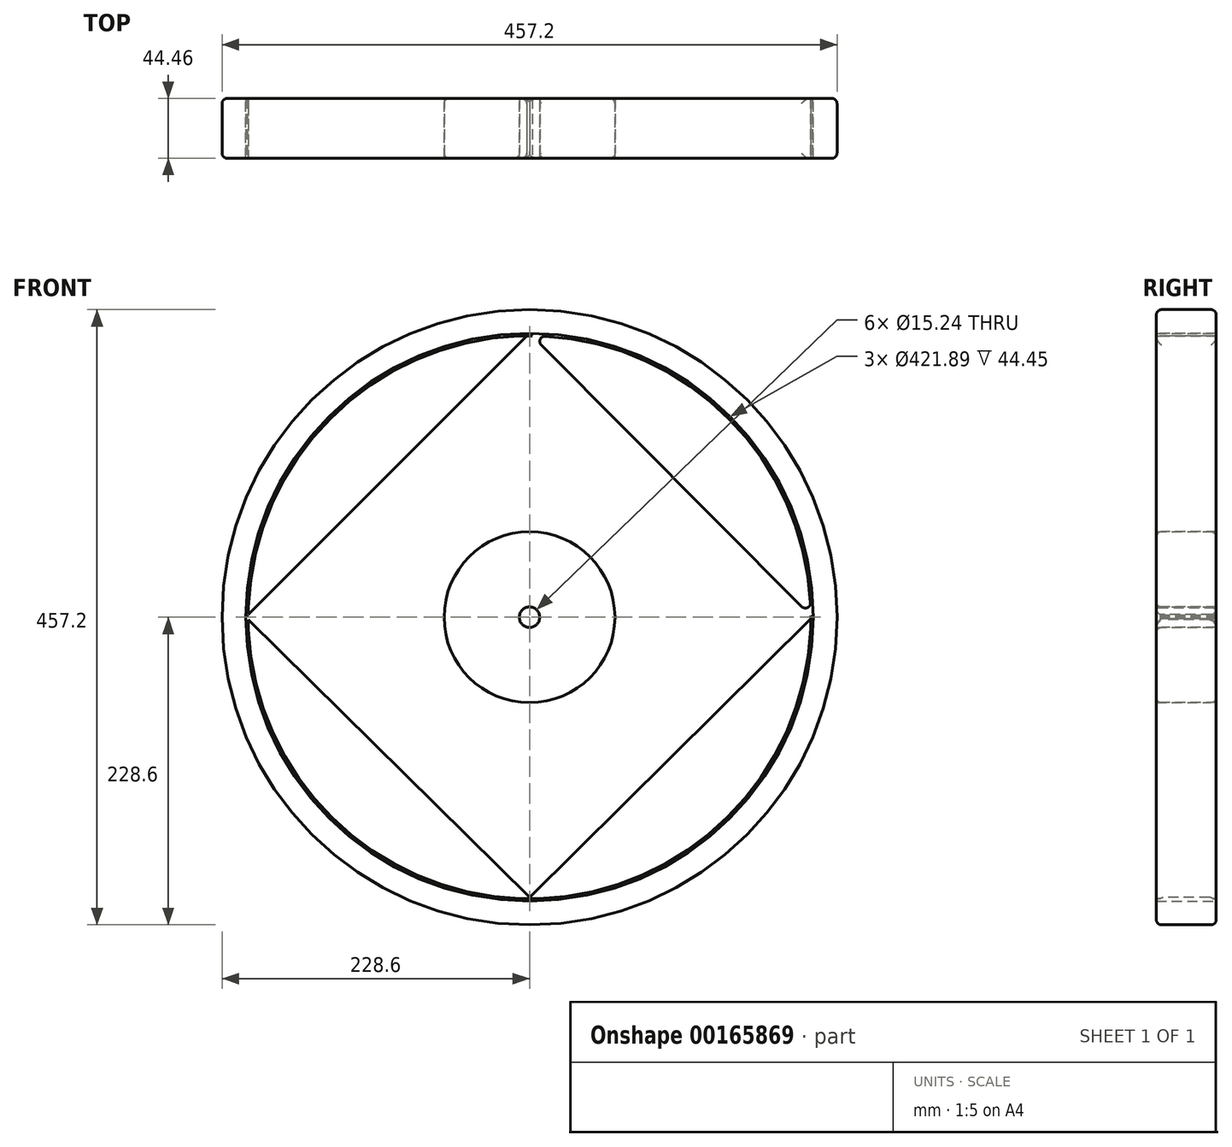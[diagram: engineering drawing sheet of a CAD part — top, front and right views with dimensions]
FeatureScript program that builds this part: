
annotation { "Feature Type Name" : "Feature", "Feature Type Description" : "" }
export const myFeature = defineFeature(function(context is Context, id is Id, definition is map)
    precondition{}
    {
        {
            var Q0;
            Q0=qCreatedBy(makeId("Front.planeOp"),FACE);
            var sketch = newSketch(context, id + "F0", { "sketchPlane" : qUnion([Q0])});
            skCircle(sketch, "E0", {"center": v(0, 0) * mm, "radius": 228.6 * mm});
            skCircle(sketch, "E1", {"center": v(0, 0) * mm, "radius": 7.62 * mm});
            skLineSegment(sketch, "E2", {"start": v(0, 0) * mm, "end": v(0, 228.6) * mm});
            skLineSegment(sketch, "E3", {"start": v(0, 0) * mm, "end": v(0, -228.6) * mm});
            skLineSegment(sketch, "E4", {"start": v(0, 0) * mm, "end": v(-228.6, 0) * mm});
            skLineSegment(sketch, "E5", {"start": v(0, 0) * mm, "end": v(228.6, 0) * mm});
            skCircle(sketch, "E6", {"center": v(0, 0) * mm, "radius": 63.5 * mm});
            skCircle(sketch, "E7", {"center": v(0, 0) * mm, "radius": 210.95 * mm});
            skSolve(sketch);
        }
        {
            var Q0;
            Q0 = qSketchRegion(id + "F0", true);
            var Q1;
            {var subQ0=sQuery(id+"F0.wireOp",EDGE,"E2");var subQ1=sQuery(id+"F0.wireOp",EDGE,"E0");var subQ2=makeQuery(id+"F0.imprint","INTERSECT",VERTEX,{"derivedFrom":[subQ1,subQ0]});Q1=makeQuery(id+"F0.imprint","IMPRINT",FACE,{"disambiguationData":[TD([[makeQuery(id+"F0.imprint","IMPRINT",EDGE,{"disambiguationData":[TD([[subQ2,-1.0]])],"derivedFrom":subQ1}),1.0]])]});}
            var Q2;
            {var subQ0=sQuery(id+"F0.wireOp",EDGE,"E2");var subQ1=sQuery(id+"F0.wireOp",EDGE,"E1");var subQ2=makeQuery(id+"F0.imprint","INTERSECT",VERTEX,{"derivedFrom":[subQ1,subQ0]});Q2=makeQuery(id+"F0.imprint","IMPRINT",FACE,{"disambiguationData":[TD([[makeQuery(id+"F0.imprint","IMPRINT",EDGE,{"disambiguationData":[TD([[subQ2,-1.0]])],"derivedFrom":subQ1}),-1.0]])]});}
            var Q3;
            {var subQ0=sQuery(id+"F0.wireOp",EDGE,"E2");var subQ1=sQuery(id+"F0.wireOp",EDGE,"E1");var subQ2=makeQuery(id+"F0.imprint","INTERSECT",VERTEX,{"derivedFrom":[subQ1,subQ0]});Q3=makeQuery(id+"F0.imprint","IMPRINT",FACE,{"disambiguationData":[TD([[makeQuery(id+"F0.imprint","IMPRINT",EDGE,{"disambiguationData":[TD([[subQ2,1.0]])],"derivedFrom":subQ1}),-1.0]])]});}
            var Q4;
            {var subQ0=sQuery(id+"F0.wireOp",EDGE,"E5");var subQ1=sQuery(id+"F0.wireOp",EDGE,"E1");var subQ2=makeQuery(id+"F0.imprint","INTERSECT",VERTEX,{"derivedFrom":[subQ1,subQ0]});Q4=makeQuery(id+"F0.imprint","IMPRINT",FACE,{"disambiguationData":[TD([[makeQuery(id+"F0.imprint","IMPRINT",EDGE,{"disambiguationData":[TD([[subQ2,1.0]])],"derivedFrom":subQ1}),-1.0]])]});}
            var Q5;
            {var subQ0=sQuery(id+"F0.wireOp",EDGE,"E4");var subQ1=sQuery(id+"F0.wireOp",EDGE,"E1");var subQ2=makeQuery(id+"F0.imprint","INTERSECT",VERTEX,{"derivedFrom":[subQ1,subQ0]});Q5=makeQuery(id+"F0.imprint","IMPRINT",FACE,{"disambiguationData":[TD([[makeQuery(id+"F0.imprint","IMPRINT",EDGE,{"disambiguationData":[TD([[subQ2,-1.0]])],"derivedFrom":subQ1}),-1.0]])]});}
            extrude(context, id + "F1", {"entities" : qUnion([Q0, Q1, Q2, Q3, Q4, Q5]), "endBound" : BoundingType.SYMMETRIC, "depth" : 44.45 * mm});
        }
        {
            var Q0;
            Q0=makeQuery(id+"F1.opExtrude","CAP_FACE",FACE,{"disambiguationData":[OSD([sQuery(id+"F0.wireOp",EDGE,"E1"),sQuery(id+"F0.wireOp",EDGE,"E6")])],"isStart":false});
            var sketch = newSketch(context, id + "F2", { "sketchPlane" : qUnion([Q0])});
            skLineSegment(sketch, "E8", {"start": v(-209.14, 0) * mm, "end": v(-211.01, 0) * mm});
            skLineSegment(sketch, "E9", {"start": v(209.14, 0) * mm, "end": v(210.23, 0) * mm});
            skLineSegment(sketch, "E10", {"start": v(0, 209.14) * mm, "end": v(0, 211.07) * mm});
            skLineSegment(sketch, "E11", {"start": v(0, -208.2) * mm, "end": v(-211.01, 0) * mm});
            skLineSegment(sketch, "E12", {"start": v(-211.01, 0) * mm, "end": v(0, 211.07) * mm});
            skLineSegment(sketch, "E13", {"start": v(0, 211.07) * mm, "end": v(210.23, 0) * mm});
            skLineSegment(sketch, "E14", {"start": v(210.23, 0) * mm, "end": v(0, -208.2) * mm});
            skCircle(sketch, "E15", {"center": v(0, 0) * mm, "radius": 209.14 * mm});
            skSolve(sketch);
        }
        {
            var Q0;
            {var subQ0=sQuery(id+"F2.wireOp",EDGE,"E14");var subQ1=sQuery(id+"F2.wireOp",EDGE,"E11");var subQ2=makeQuery(id+"F2.imprint","INTERSECT",VERTEX,{"derivedFrom":[subQ1,subQ0]});Q0=makeQuery(id+"F2.imprint","IMPRINT",FACE,{"disambiguationData":[TD([[makeQuery(id+"F2.imprint","IMPRINT",EDGE,{"disambiguationData":[TD([[subQ2,-1.0]])],"derivedFrom":subQ1}),1.0]])]});}
            var Q1;
            {var subQ0=sQuery(id+"F2.wireOp",EDGE,"E15");var subQ1=sQuery(id+"F2.wireOp",EDGE,"E12");var subQ2=makeQuery(id+"F2.imprint","INTERSECT",VERTEX,{"disambiguationData":[OD(0.0)],"derivedFrom":[subQ1,subQ0]});Q1=makeQuery(id+"F2.imprint","IMPRINT",FACE,{"disambiguationData":[TD([[makeQuery(id+"F2.imprint","IMPRINT",EDGE,{"disambiguationData":[TD([[subQ2,-1.0]])],"derivedFrom":subQ1}),1.0]])]});}
            var Q2;
            {var subQ0=sQuery(id+"F2.wireOp",EDGE,"E15");var subQ1=sQuery(id+"F2.wireOp",EDGE,"E13");var subQ2=makeQuery(id+"F2.imprint","INTERSECT",VERTEX,{"disambiguationData":[OD(0.0)],"derivedFrom":[subQ1,subQ0]});Q2=makeQuery(id+"F2.imprint","IMPRINT",FACE,{"disambiguationData":[TD([[makeQuery(id+"F2.imprint","IMPRINT",EDGE,{"disambiguationData":[TD([[subQ2,-1.0]])],"derivedFrom":subQ1}),1.0]])]});}
            var Q3;
            {var subQ0=sQuery(id+"F2.wireOp",EDGE,"E8");Q3=makeQuery(id+"F2.imprint","IMPRINT",FACE,{"disambiguationData":[TD([[makeQuery(id+"F2.imprint","IMPRINT",EDGE,{"derivedFrom":subQ0}),1.0]])]});}
            var Q4;
            {var subQ0=sQuery(id+"F2.wireOp",EDGE,"E8");Q4=makeQuery(id+"F2.imprint","IMPRINT",FACE,{"disambiguationData":[TD([[makeQuery(id+"F2.imprint","IMPRINT",EDGE,{"derivedFrom":subQ0}),-1.0]])]});}
            var Q5;
            {var subQ0=sQuery(id+"F2.wireOp",EDGE,"E9");Q5=makeQuery(id+"F2.imprint","IMPRINT",FACE,{"disambiguationData":[TD([[makeQuery(id+"F2.imprint","IMPRINT",EDGE,{"derivedFrom":subQ0}),1.0]])]});}
            var Q6;
            {var subQ0=sQuery(id+"F2.wireOp",EDGE,"E9");Q6=makeQuery(id+"F2.imprint","IMPRINT",FACE,{"disambiguationData":[TD([[makeQuery(id+"F2.imprint","IMPRINT",EDGE,{"derivedFrom":subQ0}),-1.0]])]});}
            var Q7;
            {var subQ0=sQuery(id+"F2.wireOp",EDGE,"E10");Q7=makeQuery(id+"F2.imprint","IMPRINT",FACE,{"disambiguationData":[TD([[makeQuery(id+"F2.imprint","IMPRINT",EDGE,{"derivedFrom":subQ0}),1.0]])]});}
            var Q8;
            {var subQ0=sQuery(id+"F2.wireOp",EDGE,"E10");Q8=makeQuery(id+"F2.imprint","IMPRINT",FACE,{"disambiguationData":[TD([[makeQuery(id+"F2.imprint","IMPRINT",EDGE,{"derivedFrom":subQ0}),-1.0]])]});}
            var Q9;
            Q9=makeQuery(id+"F2.imprint","IMPRINT",FACE,{"disambiguationData":[TD([[makeQuery(id+"F2.imprint","IMPRINT",EDGE,{"derivedFrom":makeQuery(id+"F1.opExtrude","CAP_EDGE",EDGE,{"disambiguationData":[OSD([sQuery(id+"F0.wireOp",EDGE,"E1")])],"isStart":false})}),-1.0]])]});
            extrude(context, id + "F3", {"entities" : qUnion([Q0, Q1, Q2, Q3, Q4, Q5, Q6, Q7, Q8, Q9]), "oppositeDirection" : true, "depth" : 44.45 * mm});
        }
        {
            var Q0;
            {var subQ0=sQuery(id+"F2.wireOp",EDGE,"E15");var subQ1=sQuery(id+"F2.wireOp",EDGE,"E13");Q0=makeQuery(id+"F3.opExtrude","SWEPT_EDGE",EDGE,{"disambiguationData":[OSD([subQ1,subQ0]),TDD([makeQuery(id+"F2.imprint","INTERSECT",VERTEX,{"disambiguationData":[OD(1.0)],"derivedFrom":[subQ1,subQ0]})]),ownerDisambiguation([makeQuery(id+"F3.opExtrude","SWEPT_BODY",BODY,{"disambiguationData":[OSD([subQ1,subQ0])]})])]});}
            var Q1;
            {var subQ0=sQuery(id+"F2.wireOp",EDGE,"E15");var subQ1=sQuery(id+"F2.wireOp",EDGE,"E13");Q1=makeQuery(id+"F3.opExtrude","SWEPT_EDGE",EDGE,{"disambiguationData":[OSD([subQ1,subQ0]),TDD([makeQuery(id+"F2.imprint","INTERSECT",VERTEX,{"disambiguationData":[OD(0.0)],"derivedFrom":[subQ1,subQ0]})]),ownerDisambiguation([makeQuery(id+"F3.opExtrude","SWEPT_BODY",BODY,{"disambiguationData":[OSD([subQ1,subQ0])]})])]});}
            var Q2;
            {var subQ0=sQuery(id+"F2.wireOp",EDGE,"E15");var subQ1=sQuery(id+"F2.wireOp",EDGE,"E11");Q2=makeQuery(id+"F3.opExtrude","SWEPT_EDGE",EDGE,{"disambiguationData":[OSD([subQ1,subQ0]),ownerDisambiguation([makeQuery(id+"F3.opExtrude","SWEPT_BODY",BODY,{"disambiguationData":[OSD([subQ1,sQuery(id+"F2.wireOp",EDGE,"E14"),subQ0])]})])]});}
            var Q3;
            Q3=makeQuery(id+"F3.opExtrude","SWEPT_EDGE",EDGE,{"disambiguationData":[OSD([sQuery(id+"F2.wireOp",EDGE,"E11"),sQuery(id+"F2.wireOp",EDGE,"E14")])]});
            var Q4;
            Q4=makeQuery(id+"F1.opExtrude","CAP_EDGE",EDGE,{"disambiguationData":[OSD([sQuery(id+"F0.wireOp",EDGE,"E6")])],"isStart":true});
            var Q5;
            Q5=makeQuery(id+"F3.opExtrude","CAP_EDGE",EDGE,{"disambiguationData":[OSD([sQuery(id+"F0.wireOp",EDGE,"E6")])],"isStart":true});
            var Q6;
            Q6=makeQuery(id+"F3.opExtrude","CAP_FACE",FACE,{"disambiguationData":[OSD([sQuery(id+"F0.wireOp",EDGE,"E6")])],"isStart":true});
            var Q7;
            Q7=makeQuery(id+"F1.opExtrude","CAP_EDGE",EDGE,{"disambiguationData":[OSD([sQuery(id+"F0.wireOp",EDGE,"E0")])],"isStart":false});
            var Q8;
            Q8=makeQuery(id+"F1.opExtrude","CAP_EDGE",EDGE,{"disambiguationData":[OSD([sQuery(id+"F0.wireOp",EDGE,"E0")])],"isStart":true});
            var Q9;
            {var subQ0=sQuery(id+"F2.wireOp",EDGE,"E15");var subQ1=sQuery(id+"F2.wireOp",EDGE,"E12");Q9=makeQuery(id+"F3.opExtrude","CAP_EDGE",EDGE,{"disambiguationData":[OSD([subQ1]),TDD([makeQuery(id+"F2.imprint","IMPRINT",EDGE,{"disambiguationData":[TD([[makeQuery(id+"F2.imprint","INTERSECT",VERTEX,{"disambiguationData":[OD(0.0)],"derivedFrom":[subQ1,subQ0]}),-1.0]])],"derivedFrom":subQ1})])],"isStart":true});}
            var Q10;
            {var subQ0=sQuery(id+"F2.wireOp",EDGE,"E15");var subQ1=sQuery(id+"F2.wireOp",EDGE,"E13");Q10=makeQuery(id+"F3.opExtrude","CAP_EDGE",EDGE,{"disambiguationData":[OSD([subQ1]),TDD([makeQuery(id+"F2.imprint","IMPRINT",EDGE,{"disambiguationData":[TD([[makeQuery(id+"F2.imprint","INTERSECT",VERTEX,{"disambiguationData":[OD(0.0)],"derivedFrom":[subQ1,subQ0]}),-1.0]])],"derivedFrom":subQ1})])],"isStart":true});}
            var Q11;
            {var subQ0=sQuery(id+"F2.wireOp",EDGE,"E14");Q11=makeQuery(id+"F3.opExtrude","CAP_EDGE",EDGE,{"disambiguationData":[OSD([subQ0]),TDD([makeQuery(id+"F2.imprint","IMPRINT",EDGE,{"disambiguationData":[TD([[makeQuery(id+"F2.imprint","INTERSECT",VERTEX,{"derivedFrom":[sQuery(id+"F2.wireOp",EDGE,"E11"),subQ0]}),1.0]])],"derivedFrom":subQ0})])],"isStart":true});}
            var Q12;
            {var subQ0=sQuery(id+"F2.wireOp",EDGE,"E11");Q12=makeQuery(id+"F3.opExtrude","CAP_EDGE",EDGE,{"disambiguationData":[OSD([subQ0]),TDD([makeQuery(id+"F2.imprint","IMPRINT",EDGE,{"disambiguationData":[TD([[makeQuery(id+"F2.imprint","INTERSECT",VERTEX,{"derivedFrom":[subQ0,sQuery(id+"F2.wireOp",EDGE,"E14")]}),-1.0]])],"derivedFrom":subQ0})])],"isStart":true});}
            var Q13;
            {var subQ0=sQuery(id+"F2.wireOp",EDGE,"E15");var subQ1=sQuery(id+"F2.wireOp",EDGE,"E13");Q13=makeQuery(id+"F3.opExtrude","CAP_EDGE",EDGE,{"disambiguationData":[OSD([subQ1]),TDD([makeQuery(id+"F2.imprint","IMPRINT",EDGE,{"disambiguationData":[TD([[makeQuery(id+"F2.imprint","INTERSECT",VERTEX,{"disambiguationData":[OD(0.0)],"derivedFrom":[subQ1,subQ0]}),-1.0]])],"derivedFrom":subQ1})])],"isStart":false});}
            var Q14;
            {var subQ0=sQuery(id+"F2.wireOp",EDGE,"E11");Q14=makeQuery(id+"F3.opExtrude","CAP_EDGE",EDGE,{"disambiguationData":[OSD([subQ0]),TDD([makeQuery(id+"F2.imprint","IMPRINT",EDGE,{"disambiguationData":[TD([[makeQuery(id+"F2.imprint","INTERSECT",VERTEX,{"derivedFrom":[subQ0,sQuery(id+"F2.wireOp",EDGE,"E14")]}),-1.0]])],"derivedFrom":subQ0})])],"isStart":false});}
            var Q15;
            {var subQ0=sQuery(id+"F2.wireOp",EDGE,"E14");Q15=makeQuery(id+"F3.opExtrude","CAP_EDGE",EDGE,{"disambiguationData":[OSD([subQ0]),TDD([makeQuery(id+"F2.imprint","IMPRINT",EDGE,{"disambiguationData":[TD([[makeQuery(id+"F2.imprint","INTERSECT",VERTEX,{"derivedFrom":[sQuery(id+"F2.wireOp",EDGE,"E11"),subQ0]}),1.0]])],"derivedFrom":subQ0})])],"isStart":false});}
            var Q16;
            {var subQ0=sQuery(id+"F2.wireOp",EDGE,"E15");var subQ1=sQuery(id+"F2.wireOp",EDGE,"E12");Q16=makeQuery(id+"F3.opExtrude","CAP_EDGE",EDGE,{"disambiguationData":[OSD([subQ1]),TDD([makeQuery(id+"F2.imprint","IMPRINT",EDGE,{"disambiguationData":[TD([[makeQuery(id+"F2.imprint","INTERSECT",VERTEX,{"disambiguationData":[OD(0.0)],"derivedFrom":[subQ1,subQ0]}),-1.0]])],"derivedFrom":subQ1})])],"isStart":false});}
            fillet(context, id + "F4", {"entities" : qUnion([Q0, Q1, Q2, Q3, Q4, Q5, Q6, Q7, Q8, Q9, Q10, Q11, Q12, Q13, Q14, Q15, Q16]), "radius" : 3.8 * mm, "tangentPropagation" : true, "allowEdgeOverflow" : false});
        }
        {
            var Q0;
            {var subQ0=sQuery(id+"F2.wireOp",EDGE,"E15");var subQ1=sQuery(id+"F2.wireOp",EDGE,"E13");Q0=makeQuery(id+"F3.opExtrude","CAP_EDGE",EDGE,{"disambiguationData":[OSD([subQ1]),TDD([makeQuery(id+"F2.imprint","IMPRINT",EDGE,{"disambiguationData":[TD([[makeQuery(id+"F2.imprint","INTERSECT",VERTEX,{"disambiguationData":[OD(0.0)],"derivedFrom":[subQ1,subQ0]}),-1.0]])],"derivedFrom":subQ1})])],"isStart":true});}
            var Q1;
            {var subQ0=sQuery(id+"F2.wireOp",EDGE,"E14");Q1=makeQuery(id+"F3.opExtrude","CAP_EDGE",EDGE,{"disambiguationData":[OSD([subQ0]),TDD([makeQuery(id+"F2.imprint","IMPRINT",EDGE,{"disambiguationData":[TD([[makeQuery(id+"F2.imprint","INTERSECT",VERTEX,{"derivedFrom":[sQuery(id+"F2.wireOp",EDGE,"E11"),subQ0]}),1.0]])],"derivedFrom":subQ0})])],"isStart":true});}
            var Q2;
            {var subQ0=sQuery(id+"F2.wireOp",EDGE,"E11");Q2=makeQuery(id+"F3.opExtrude","CAP_EDGE",EDGE,{"disambiguationData":[OSD([subQ0]),TDD([makeQuery(id+"F2.imprint","IMPRINT",EDGE,{"disambiguationData":[TD([[makeQuery(id+"F2.imprint","INTERSECT",VERTEX,{"derivedFrom":[subQ0,sQuery(id+"F2.wireOp",EDGE,"E14")]}),-1.0]])],"derivedFrom":subQ0})])],"isStart":true});}
            var Q3;
            {var subQ0=sQuery(id+"F2.wireOp",EDGE,"E15");var subQ1=sQuery(id+"F2.wireOp",EDGE,"E12");Q3=makeQuery(id+"F3.opExtrude","CAP_EDGE",EDGE,{"disambiguationData":[OSD([subQ1]),TDD([makeQuery(id+"F2.imprint","IMPRINT",EDGE,{"disambiguationData":[TD([[makeQuery(id+"F2.imprint","INTERSECT",VERTEX,{"disambiguationData":[OD(0.0)],"derivedFrom":[subQ1,subQ0]}),-1.0]])],"derivedFrom":subQ1})])],"isStart":true});}
            var Q4;
            Q4=makeQuery(id+"F1.opExtrude","CAP_EDGE",EDGE,{"disambiguationData":[OSD([sQuery(id+"F0.wireOp",EDGE,"E0")])],"isStart":false});
            var Q5;
            Q5=makeQuery(id+"F1.opExtrude","CAP_EDGE",EDGE,{"disambiguationData":[OSD([sQuery(id+"F0.wireOp",EDGE,"E0")])],"isStart":true});
            var Q6;
            {var subQ0=sQuery(id+"F2.wireOp",EDGE,"E14");Q6=makeQuery(id+"F3.opExtrude","CAP_EDGE",EDGE,{"disambiguationData":[OSD([subQ0]),TDD([makeQuery(id+"F2.imprint","IMPRINT",EDGE,{"disambiguationData":[TD([[makeQuery(id+"F2.imprint","INTERSECT",VERTEX,{"derivedFrom":[sQuery(id+"F2.wireOp",EDGE,"E11"),subQ0]}),1.0]])],"derivedFrom":subQ0})])],"isStart":false});}
            var Q7;
            Q7=makeQuery(id+"F1.opExtrude","CAP_EDGE",EDGE,{"disambiguationData":[OSD([sQuery(id+"F0.wireOp",EDGE,"E6")])],"isStart":true});
            var Q8;
            {var subQ0=sQuery(id+"F2.wireOp",EDGE,"E15");var subQ1=sQuery(id+"F2.wireOp",EDGE,"E12");Q8=makeQuery(id+"F3.opExtrude","CAP_EDGE",EDGE,{"disambiguationData":[OSD([subQ1]),TDD([makeQuery(id+"F2.imprint","IMPRINT",EDGE,{"disambiguationData":[TD([[makeQuery(id+"F2.imprint","INTERSECT",VERTEX,{"disambiguationData":[OD(0.0)],"derivedFrom":[subQ1,subQ0]}),-1.0]])],"derivedFrom":subQ1})])],"isStart":false});}
            var Q9;
            {var subQ0=sQuery(id+"F2.wireOp",EDGE,"E11");Q9=makeQuery(id+"F3.opExtrude","CAP_EDGE",EDGE,{"disambiguationData":[OSD([subQ0]),TDD([makeQuery(id+"F2.imprint","IMPRINT",EDGE,{"disambiguationData":[TD([[makeQuery(id+"F2.imprint","INTERSECT",VERTEX,{"derivedFrom":[subQ0,sQuery(id+"F2.wireOp",EDGE,"E14")]}),-1.0]])],"derivedFrom":subQ0})])],"isStart":false});}
            fillet(context, id + "F5", {"entities" : qUnion([Q0, Q1, Q2, Q3, Q4, Q5, Q6, Q7, Q8, Q9]), "radius" : 5.08 * mm, "tangentPropagation" : true, "allowEdgeOverflow" : false});
        }
    });
